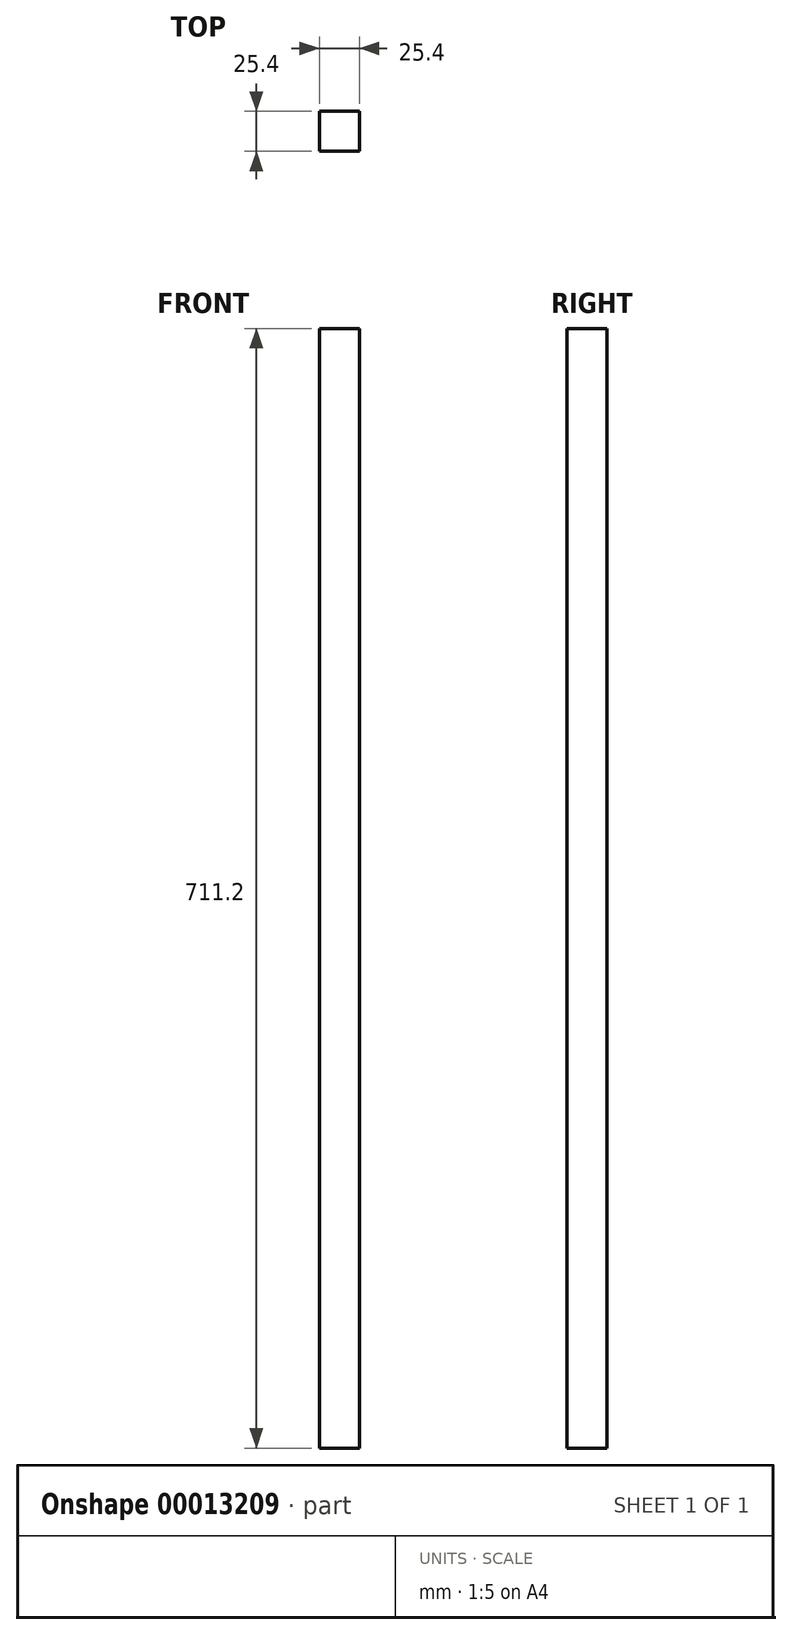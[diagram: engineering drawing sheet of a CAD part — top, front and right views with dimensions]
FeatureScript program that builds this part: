
annotation { "Feature Type Name" : "Feature", "Feature Type Description" : "" }
export const myFeature = defineFeature(function(context is Context, id is Id, definition is map)
    precondition{}
    {
        {
            var Q0;
            Q0=qCreatedBy(makeId("Top.planeOp"),FACE);
            var sketch = newSketch(context, id + "F0", { "sketchPlane" : qUnion([Q0])});
            skLineSegment(sketch, "E0.rect.bottom", {"start": v(12.7, -12.7) * mm, "end": v(-12.7, -12.7) * mm});
            skLineSegment(sketch, "E0.rect.top", {"start": v(12.7, 12.7) * mm, "end": v(-12.7, 12.7) * mm});
            skLineSegment(sketch, "E0.rect.left", {"start": v(12.7, -12.7) * mm, "end": v(12.7, 12.7) * mm});
            skLineSegment(sketch, "E0.rect.right", {"start": v(-12.7, -12.7) * mm, "end": v(-12.7, 12.7) * mm});
            skPoint(sketch, "E0.rect.middle", {"position": v(0, 0) * mm});
            skSolve(sketch);
        }
        {
            var Q0;
            Q0 = qSketchRegion(id + "F0", true);
            extrude(context, id + "F1", {"entities" : qUnion([Q0]), "depth" : 711.2 * mm});
        }
    });
